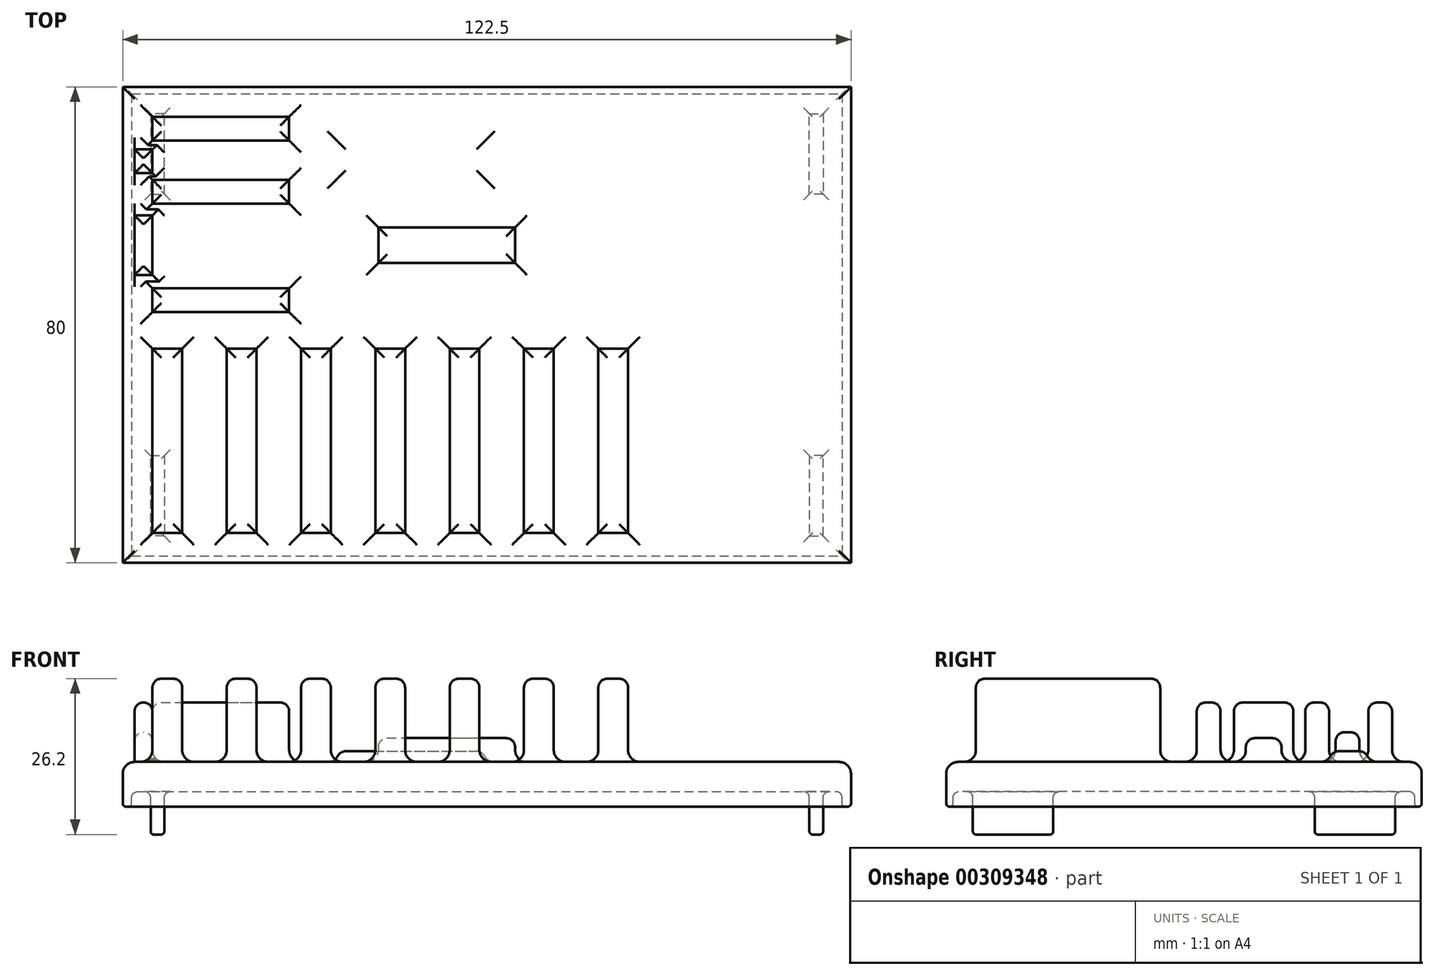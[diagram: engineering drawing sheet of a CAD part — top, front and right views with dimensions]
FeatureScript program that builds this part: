
annotation { "Feature Type Name" : "Feature", "Feature Type Description" : "" }
export const myFeature = defineFeature(function(context is Context, id is Id, definition is map)
    precondition{}
    {
        {
            var Q0;
            Q0=qCreatedBy(makeId("Top.planeOp"),FACE);
            var sketch = newSketch(context, id + "F0", { "sketchPlane" : qUnion([Q0])});
            skLineSegment(sketch, "E0.bottom", {"start": v(-61.25, 40) * mm, "end": v(61.25, 40) * mm});
            skLineSegment(sketch, "E0.top", {"start": v(-61.25, -40) * mm, "end": v(61.25, -40) * mm});
            skLineSegment(sketch, "E0.left", {"start": v(-61.25, 40) * mm, "end": v(-61.25, -40) * mm});
            skLineSegment(sketch, "E0.right", {"start": v(61.25, 40) * mm, "end": v(61.25, -40) * mm});
            skPoint(sketch, "E0.middle", {"position": v(0, 0) * mm});
            skLineSegment(sketch, "E1.bottom", {"start": v(-59.75, 38.85) * mm, "end": v(59.75, 38.85) * mm});
            skLineSegment(sketch, "E1.top", {"start": v(-59.75, -38.85) * mm, "end": v(59.75, -38.85) * mm});
            skLineSegment(sketch, "E1.left", {"start": v(-59.75, 38.85) * mm, "end": v(-59.75, -38.85) * mm});
            skLineSegment(sketch, "E1.right", {"start": v(59.75, 38.85) * mm, "end": v(59.75, -38.85) * mm});
            skLineSegment(sketch, "E2", {"start": v(61.25, -40) * mm, "end": v(61.25, -22) * mm});
            skLineSegment(sketch, "E3", {"start": v(61.25, -22) * mm, "end": v(54.25, -22) * mm});
            skLineSegment(sketch, "E4", {"start": v(54.25, -22) * mm, "end": v(54.25, -35.5) * mm});
            skLineSegment(sketch, "E5", {"start": v(54.25, -35.5) * mm, "end": v(56.55, -35.5) * mm});
            skLineSegment(sketch, "E6", {"start": v(56.55, -35.5) * mm, "end": v(56.55, -22) * mm});
            skLineSegment(sketch, "E7.MirrorCS", {"start": v(-56.55, -35.5) * mm, "end": v(-56.55, -22) * mm});
            skLineSegment(sketch, "E8.MirrorCS", {"start": v(-61.25, -22) * mm, "end": v(-54.25, -22) * mm});
            skLineSegment(sketch, "E9.MirrorCS", {"start": v(-54.25, -22) * mm, "end": v(-54.25, -35.5) * mm});
            skLineSegment(sketch, "E10.MirrorCS", {"start": v(-54.25, -35.5) * mm, "end": v(-56.55, -35.5) * mm});
            skLineSegment(sketch, "E11.MirrorCS", {"start": v(56.55, 35.5) * mm, "end": v(56.55, 22) * mm});
            skLineSegment(sketch, "E12.MirrorCS", {"start": v(54.25, 35.5) * mm, "end": v(56.55, 35.5) * mm});
            skLineSegment(sketch, "E13.MirrorCS", {"start": v(54.25, 22) * mm, "end": v(54.25, 35.5) * mm});
            skLineSegment(sketch, "E14.MirrorCS", {"start": v(-54.25, 35.5) * mm, "end": v(-56.55, 35.5) * mm});
            skLineSegment(sketch, "E15.MirrorCS", {"start": v(-54.25, 22) * mm, "end": v(-54.25, 35.5) * mm});
            skLineSegment(sketch, "E16.MirrorCS", {"start": v(-56.55, 35.5) * mm, "end": v(-56.55, 22) * mm});
            skLineSegment(sketch, "E17.MirrorCS", {"start": v(-61.25, 22) * mm, "end": v(-54.25, 22) * mm});
            skLineSegment(sketch, "E18.MirrorCS", {"start": v(61.25, 22) * mm, "end": v(54.25, 22) * mm});
            skSolve(sketch);
        }
        {
            var Q0;
            {var subQ0=sQuery(id+"F0.wireOp",EDGE,"E4");Q0=makeQuery(id+"F0.imprint","IMPRINT",FACE,{"disambiguationData":[TD([[makeQuery(id+"F0.imprint","IMPRINT",EDGE,{"derivedFrom":subQ0}),1.0]])]});}
            var Q1;
            {var subQ0=sQuery(id+"F0.wireOp",EDGE,"E9.MirrorCS");Q1=makeQuery(id+"F0.imprint","IMPRINT",FACE,{"disambiguationData":[TD([[makeQuery(id+"F0.imprint","IMPRINT",EDGE,{"derivedFrom":subQ0}),-1.0]])]});}
            var Q2;
            {var subQ0=sQuery(id+"F0.wireOp",EDGE,"E11.MirrorCS");Q2=makeQuery(id+"F0.imprint","IMPRINT",FACE,{"disambiguationData":[TD([[makeQuery(id+"F0.imprint","IMPRINT",EDGE,{"derivedFrom":subQ0}),-1.0]])]});}
            var Q3;
            Q3=makeQuery(id+"F0.imprint","IMPRINT",FACE,{"disambiguationData":[TD([[makeQuery(id+"F0.imprint","IMPRINT",EDGE,{"derivedFrom":sQuery(id+"F0.wireOp",EDGE,"E14.MirrorCS")}),1.0]])]});
            var Q4;
            {var subQ2=sQuery(id+"F0.wireOp",EDGE,"E0.bottom");Q4=makeQuery(id+"F0.imprint","IMPRINT",FACE,{"disambiguationData":[TD([[makeQuery(id+"F0.imprint","IMPRINT",EDGE,{"derivedFrom":subQ2}),-1.0]])]});}
            var Q5;
            {var subQ2=sQuery(id+"F0.wireOp",EDGE,"E0.top");Q5=makeQuery(id+"F0.imprint","IMPRINT",FACE,{"disambiguationData":[TD([[makeQuery(id+"F0.imprint","IMPRINT",EDGE,{"derivedFrom":subQ2}),1.0]])]});}
            var Q6;
            {var subQ0=sQuery(id+"F0.wireOp",EDGE,"E8.MirrorCS");var subQ1=sQuery(id+"F0.wireOp",EDGE,"E0.left");var subQ2=makeQuery(id+"F0.imprint","INTERSECT",VERTEX,{"derivedFrom":[subQ1,subQ0]});Q6=makeQuery(id+"F0.imprint","IMPRINT",FACE,{"disambiguationData":[TD([[makeQuery(id+"F0.imprint","IMPRINT",EDGE,{"disambiguationData":[TD([[subQ2,1.0]])],"derivedFrom":subQ1}),1.0]])]});}
            var Q7;
            {var subQ10=sQuery(id+"F0.wireOp",EDGE,"E1.bottom");Q7=makeQuery(id+"F0.imprint","IMPRINT",FACE,{"disambiguationData":[TD([[makeQuery(id+"F0.imprint","IMPRINT",EDGE,{"derivedFrom":subQ10}),-1.0]])]});}
            var Q8;
            {var subQ3=sQuery(id+"F0.wireOp",EDGE,"E18.MirrorCS");var subQ5=sQuery(id+"F0.wireOp",EDGE,"E1.right");var subQ7=makeQuery(id+"F0.imprint","INTERSECT",VERTEX,{"derivedFrom":[subQ5,subQ3]});Q8=makeQuery(id+"F0.imprint","IMPRINT",FACE,{"disambiguationData":[TD([[makeQuery(id+"F0.imprint","IMPRINT",EDGE,{"disambiguationData":[TD([[subQ7,-1.0]])],"derivedFrom":subQ5}),1.0]])]});}
            extrude(context, id + "F1", {"entities" : qUnion([Q0, Q1, Q2, Q3, Q4, Q5, Q6, Q7, Q8]), "oppositeDirection" : true, "depth" : 5 * mm});
        }
        {
            var Q0;
            {var subQ0=sQuery(id+"F0.wireOp",EDGE,"E9.MirrorCS");Q0=makeQuery(id+"F0.imprint","IMPRINT",FACE,{"disambiguationData":[TD([[makeQuery(id+"F0.imprint","IMPRINT",EDGE,{"derivedFrom":subQ0}),-1.0]])]});}
            var Q1;
            Q1=makeQuery(id+"F0.imprint","IMPRINT",FACE,{"disambiguationData":[TD([[makeQuery(id+"F0.imprint","IMPRINT",EDGE,{"derivedFrom":sQuery(id+"F0.wireOp",EDGE,"E14.MirrorCS")}),1.0]])]});
            var Q2;
            {var subQ0=sQuery(id+"F0.wireOp",EDGE,"E11.MirrorCS");Q2=makeQuery(id+"F0.imprint","IMPRINT",FACE,{"disambiguationData":[TD([[makeQuery(id+"F0.imprint","IMPRINT",EDGE,{"derivedFrom":subQ0}),-1.0]])]});}
            var Q3;
            {var subQ0=sQuery(id+"F0.wireOp",EDGE,"E4");Q3=makeQuery(id+"F0.imprint","IMPRINT",FACE,{"disambiguationData":[TD([[makeQuery(id+"F0.imprint","IMPRINT",EDGE,{"derivedFrom":subQ0}),1.0]])]});}
            extrude(context, id + "F2", {"entities" : qUnion([Q0, Q1, Q2, Q3]), "operationType" : NewBodyOperationType.ADD, "oppositeDirection" : true, "depth" : (7.2 + 5) * mm});
        }
        {
            var Q0;
            {var subQ0=sQuery(id+"F0.wireOp",EDGE,"E8.MirrorCS");var subQ1=sQuery(id+"F0.wireOp",EDGE,"E0.left");var subQ2=makeQuery(id+"F0.imprint","INTERSECT",VERTEX,{"derivedFrom":[subQ1,subQ0]});Q0=makeQuery(id+"F0.imprint","IMPRINT",FACE,{"disambiguationData":[TD([[makeQuery(id+"F0.imprint","IMPRINT",EDGE,{"disambiguationData":[TD([[subQ2,1.0]])],"derivedFrom":subQ1}),1.0]])]});}
            var Q1;
            {var subQ2=sQuery(id+"F0.wireOp",EDGE,"E0.bottom");Q1=makeQuery(id+"F0.imprint","IMPRINT",FACE,{"disambiguationData":[TD([[makeQuery(id+"F0.imprint","IMPRINT",EDGE,{"derivedFrom":subQ2}),-1.0]])]});}
            var Q2;
            {var subQ2=sQuery(id+"F0.wireOp",EDGE,"E0.top");Q2=makeQuery(id+"F0.imprint","IMPRINT",FACE,{"disambiguationData":[TD([[makeQuery(id+"F0.imprint","IMPRINT",EDGE,{"derivedFrom":subQ2}),1.0]])]});}
            var Q3;
            {var subQ3=sQuery(id+"F0.wireOp",EDGE,"E18.MirrorCS");var subQ5=sQuery(id+"F0.wireOp",EDGE,"E1.right");var subQ7=makeQuery(id+"F0.imprint","INTERSECT",VERTEX,{"derivedFrom":[subQ5,subQ3]});Q3=makeQuery(id+"F0.imprint","IMPRINT",FACE,{"disambiguationData":[TD([[makeQuery(id+"F0.imprint","IMPRINT",EDGE,{"disambiguationData":[TD([[subQ7,-1.0]])],"derivedFrom":subQ5}),1.0]])]});}
            extrude(context, id + "F3", {"entities" : qUnion([Q0, Q1, Q2, Q3]), "operationType" : NewBodyOperationType.ADD, "oppositeDirection" : true, "depth" : (2.5 + 5) * mm});
        }
        {
            var Q0;
            Q0=makeQuery(id+"F1.opExtrude","CAP_FACE",FACE,{"disambiguationData":[OSD([sQuery(id+"F0.wireOp",EDGE,"E0.bottom"),sQuery(id+"F0.wireOp",EDGE,"E0.top"),sQuery(id+"F0.wireOp",EDGE,"E0.left"),sQuery(id+"F0.wireOp",EDGE,"E0.right"),sQuery(id+"F0.wireOp",EDGE,"E2")])],"isStart":true});
            fillet(context, id + "F4", {"entities" : qUnion([Q0]), "radius" : 2 * mm, "tangentPropagation" : true, "allowEdgeOverflow" : false});
        }
        {
            var Q0;
            Q0=makeQuery(id+"F2.opExtrude","CAP_FACE",FACE,{"disambiguationData":[OSD([sQuery(id+"F0.wireOp",EDGE,"E8.MirrorCS"),sQuery(id+"F0.wireOp",EDGE,"E9.MirrorCS"),sQuery(id+"F0.wireOp",EDGE,"E10.MirrorCS"),sQuery(id+"F0.wireOp",EDGE,"E7.MirrorCS")])],"isStart":false});
            var Q1;
            Q1=makeQuery(id+"F3.opExtrude","CAP_FACE",FACE,{"disambiguationData":[OSD([sQuery(id+"F0.wireOp",EDGE,"E0.bottom"),sQuery(id+"F0.wireOp",EDGE,"E0.top"),sQuery(id+"F0.wireOp",EDGE,"E0.left"),sQuery(id+"F0.wireOp",EDGE,"E0.right"),sQuery(id+"F0.wireOp",EDGE,"E1.bottom"),sQuery(id+"F0.wireOp",EDGE,"E1.top"),sQuery(id+"F0.wireOp",EDGE,"E1.left"),sQuery(id+"F0.wireOp",EDGE,"E1.right"),sQuery(id+"F0.wireOp",EDGE,"E2")])],"isStart":false});
            var Q2;
            Q2=makeQuery(id+"F2.opExtrude","CAP_FACE",FACE,{"disambiguationData":[OSD([sQuery(id+"F0.wireOp",EDGE,"E14.MirrorCS"),sQuery(id+"F0.wireOp",EDGE,"E16.MirrorCS"),sQuery(id+"F0.wireOp",EDGE,"E15.MirrorCS"),sQuery(id+"F0.wireOp",EDGE,"E17.MirrorCS")])],"isStart":false});
            var Q3;
            Q3=makeQuery(id+"F2.opExtrude","CAP_FACE",FACE,{"disambiguationData":[OSD([sQuery(id+"F0.wireOp",EDGE,"E11.MirrorCS"),sQuery(id+"F0.wireOp",EDGE,"E12.MirrorCS"),sQuery(id+"F0.wireOp",EDGE,"E13.MirrorCS"),sQuery(id+"F0.wireOp",EDGE,"E18.MirrorCS")])],"isStart":false});
            var Q4;
            Q4=makeQuery(id+"F2.opExtrude","CAP_FACE",FACE,{"disambiguationData":[OSD([sQuery(id+"F0.wireOp",EDGE,"E3"),sQuery(id+"F0.wireOp",EDGE,"E4"),sQuery(id+"F0.wireOp",EDGE,"E5"),sQuery(id+"F0.wireOp",EDGE,"E6")])],"isStart":false});
            fillet(context, id + "F5", {"entities" : qUnion([Q0, Q1, Q2, Q3, Q4]), "radius" : .5 * mm, "tangentPropagation" : true, "allowEdgeOverflow" : false});
        }
        {
            var Q0;
            Q0=makeQuery(id+"F2.boolean.opBoolean","INTERSECT",EDGE,{"derivedFrom":[makeQuery(id+"F1.opExtrude","CAP_FACE",FACE,{"disambiguationData":[OSD([sQuery(id+"F0.wireOp",EDGE,"E0.bottom"),sQuery(id+"F0.wireOp",EDGE,"E0.top"),sQuery(id+"F0.wireOp",EDGE,"E0.left"),sQuery(id+"F0.wireOp",EDGE,"E0.right"),sQuery(id+"F0.wireOp",EDGE,"E2")])],"isStart":false}),makeQuery(id+"F2.opExtrude","SWEPT_FACE",FACE,{"disambiguationData":[OSD([sQuery(id+"F0.wireOp",EDGE,"E9.MirrorCS")])]})]});
            var Q1;
            Q1=makeQuery(id+"F2.boolean.opBoolean","INTERSECT",EDGE,{"derivedFrom":[makeQuery(id+"F1.opExtrude","CAP_FACE",FACE,{"disambiguationData":[OSD([sQuery(id+"F0.wireOp",EDGE,"E0.bottom"),sQuery(id+"F0.wireOp",EDGE,"E0.top"),sQuery(id+"F0.wireOp",EDGE,"E0.left"),sQuery(id+"F0.wireOp",EDGE,"E0.right"),sQuery(id+"F0.wireOp",EDGE,"E2")])],"isStart":false}),makeQuery(id+"F2.opExtrude","SWEPT_FACE",FACE,{"disambiguationData":[OSD([sQuery(id+"F0.wireOp",EDGE,"E8.MirrorCS")])]})]});
            var Q2;
            Q2=makeQuery(id+"F2.boolean.opBoolean","INTERSECT",EDGE,{"derivedFrom":[makeQuery(id+"F1.opExtrude","CAP_FACE",FACE,{"disambiguationData":[OSD([sQuery(id+"F0.wireOp",EDGE,"E0.bottom"),sQuery(id+"F0.wireOp",EDGE,"E0.top"),sQuery(id+"F0.wireOp",EDGE,"E0.left"),sQuery(id+"F0.wireOp",EDGE,"E0.right"),sQuery(id+"F0.wireOp",EDGE,"E2")])],"isStart":false}),makeQuery(id+"F2.opExtrude","SWEPT_FACE",FACE,{"disambiguationData":[OSD([sQuery(id+"F0.wireOp",EDGE,"E7.MirrorCS")])]})]});
            var Q3;
            Q3=makeQuery(id+"F2.boolean.opBoolean","INTERSECT",EDGE,{"derivedFrom":[makeQuery(id+"F1.opExtrude","CAP_FACE",FACE,{"disambiguationData":[OSD([sQuery(id+"F0.wireOp",EDGE,"E0.bottom"),sQuery(id+"F0.wireOp",EDGE,"E0.top"),sQuery(id+"F0.wireOp",EDGE,"E0.left"),sQuery(id+"F0.wireOp",EDGE,"E0.right"),sQuery(id+"F0.wireOp",EDGE,"E2")])],"isStart":false}),makeQuery(id+"F2.opExtrude","SWEPT_FACE",FACE,{"disambiguationData":[OSD([sQuery(id+"F0.wireOp",EDGE,"E10.MirrorCS")])]})]});
            var Q4;
            Q4=makeQuery(id+"F2.boolean.opBoolean","INTERSECT",EDGE,{"derivedFrom":[makeQuery(id+"F1.opExtrude","CAP_FACE",FACE,{"disambiguationData":[OSD([sQuery(id+"F0.wireOp",EDGE,"E0.bottom"),sQuery(id+"F0.wireOp",EDGE,"E0.top"),sQuery(id+"F0.wireOp",EDGE,"E0.left"),sQuery(id+"F0.wireOp",EDGE,"E0.right"),sQuery(id+"F0.wireOp",EDGE,"E2")])],"isStart":false}),makeQuery(id+"F2.opExtrude","SWEPT_FACE",FACE,{"disambiguationData":[OSD([sQuery(id+"F0.wireOp",EDGE,"E16.MirrorCS")])]})]});
            var Q5;
            Q5=makeQuery(id+"F2.boolean.opBoolean","INTERSECT",EDGE,{"derivedFrom":[makeQuery(id+"F1.opExtrude","CAP_FACE",FACE,{"disambiguationData":[OSD([sQuery(id+"F0.wireOp",EDGE,"E0.bottom"),sQuery(id+"F0.wireOp",EDGE,"E0.top"),sQuery(id+"F0.wireOp",EDGE,"E0.left"),sQuery(id+"F0.wireOp",EDGE,"E0.right"),sQuery(id+"F0.wireOp",EDGE,"E2")])],"isStart":false}),makeQuery(id+"F2.opExtrude","SWEPT_FACE",FACE,{"disambiguationData":[OSD([sQuery(id+"F0.wireOp",EDGE,"E17.MirrorCS")])]})]});
            var Q6;
            Q6=makeQuery(id+"F2.boolean.opBoolean","INTERSECT",EDGE,{"derivedFrom":[makeQuery(id+"F1.opExtrude","CAP_FACE",FACE,{"disambiguationData":[OSD([sQuery(id+"F0.wireOp",EDGE,"E0.bottom"),sQuery(id+"F0.wireOp",EDGE,"E0.top"),sQuery(id+"F0.wireOp",EDGE,"E0.left"),sQuery(id+"F0.wireOp",EDGE,"E0.right"),sQuery(id+"F0.wireOp",EDGE,"E2")])],"isStart":false}),makeQuery(id+"F2.opExtrude","SWEPT_FACE",FACE,{"disambiguationData":[OSD([sQuery(id+"F0.wireOp",EDGE,"E15.MirrorCS")])]})]});
            var Q7;
            Q7=makeQuery(id+"F2.boolean.opBoolean","INTERSECT",EDGE,{"derivedFrom":[makeQuery(id+"F1.opExtrude","CAP_FACE",FACE,{"disambiguationData":[OSD([sQuery(id+"F0.wireOp",EDGE,"E0.bottom"),sQuery(id+"F0.wireOp",EDGE,"E0.top"),sQuery(id+"F0.wireOp",EDGE,"E0.left"),sQuery(id+"F0.wireOp",EDGE,"E0.right"),sQuery(id+"F0.wireOp",EDGE,"E2")])],"isStart":false}),makeQuery(id+"F2.opExtrude","SWEPT_FACE",FACE,{"disambiguationData":[OSD([sQuery(id+"F0.wireOp",EDGE,"E14.MirrorCS")])]})]});
            var Q8;
            Q8=makeQuery(id+"F2.boolean.opBoolean","INTERSECT",EDGE,{"derivedFrom":[makeQuery(id+"F1.opExtrude","CAP_FACE",FACE,{"disambiguationData":[OSD([sQuery(id+"F0.wireOp",EDGE,"E0.bottom"),sQuery(id+"F0.wireOp",EDGE,"E0.top"),sQuery(id+"F0.wireOp",EDGE,"E0.left"),sQuery(id+"F0.wireOp",EDGE,"E0.right"),sQuery(id+"F0.wireOp",EDGE,"E2")])],"isStart":false}),makeQuery(id+"F2.opExtrude","SWEPT_FACE",FACE,{"disambiguationData":[OSD([sQuery(id+"F0.wireOp",EDGE,"E13.MirrorCS")])]})]});
            var Q9;
            Q9=makeQuery(id+"F2.boolean.opBoolean","INTERSECT",EDGE,{"derivedFrom":[makeQuery(id+"F1.opExtrude","CAP_FACE",FACE,{"disambiguationData":[OSD([sQuery(id+"F0.wireOp",EDGE,"E0.bottom"),sQuery(id+"F0.wireOp",EDGE,"E0.top"),sQuery(id+"F0.wireOp",EDGE,"E0.left"),sQuery(id+"F0.wireOp",EDGE,"E0.right"),sQuery(id+"F0.wireOp",EDGE,"E2")])],"isStart":false}),makeQuery(id+"F2.opExtrude","SWEPT_FACE",FACE,{"disambiguationData":[OSD([sQuery(id+"F0.wireOp",EDGE,"E12.MirrorCS")])]})]});
            var Q10;
            Q10=makeQuery(id+"F2.boolean.opBoolean","INTERSECT",EDGE,{"derivedFrom":[makeQuery(id+"F1.opExtrude","CAP_FACE",FACE,{"disambiguationData":[OSD([sQuery(id+"F0.wireOp",EDGE,"E0.bottom"),sQuery(id+"F0.wireOp",EDGE,"E0.top"),sQuery(id+"F0.wireOp",EDGE,"E0.left"),sQuery(id+"F0.wireOp",EDGE,"E0.right"),sQuery(id+"F0.wireOp",EDGE,"E2")])],"isStart":false}),makeQuery(id+"F2.opExtrude","SWEPT_FACE",FACE,{"disambiguationData":[OSD([sQuery(id+"F0.wireOp",EDGE,"E11.MirrorCS")])]})]});
            var Q11;
            Q11=makeQuery(id+"F2.boolean.opBoolean","INTERSECT",EDGE,{"derivedFrom":[makeQuery(id+"F1.opExtrude","CAP_FACE",FACE,{"disambiguationData":[OSD([sQuery(id+"F0.wireOp",EDGE,"E0.bottom"),sQuery(id+"F0.wireOp",EDGE,"E0.top"),sQuery(id+"F0.wireOp",EDGE,"E0.left"),sQuery(id+"F0.wireOp",EDGE,"E0.right"),sQuery(id+"F0.wireOp",EDGE,"E2")])],"isStart":false}),makeQuery(id+"F2.opExtrude","SWEPT_FACE",FACE,{"disambiguationData":[OSD([sQuery(id+"F0.wireOp",EDGE,"E18.MirrorCS")])]})]});
            var Q12;
            Q12=makeQuery(id+"F2.boolean.opBoolean","INTERSECT",EDGE,{"derivedFrom":[makeQuery(id+"F1.opExtrude","CAP_FACE",FACE,{"disambiguationData":[OSD([sQuery(id+"F0.wireOp",EDGE,"E0.bottom"),sQuery(id+"F0.wireOp",EDGE,"E0.top"),sQuery(id+"F0.wireOp",EDGE,"E0.left"),sQuery(id+"F0.wireOp",EDGE,"E0.right"),sQuery(id+"F0.wireOp",EDGE,"E2")])],"isStart":false}),makeQuery(id+"F2.opExtrude","SWEPT_FACE",FACE,{"disambiguationData":[OSD([sQuery(id+"F0.wireOp",EDGE,"E5")])]})]});
            var Q13;
            Q13=makeQuery(id+"F2.boolean.opBoolean","INTERSECT",EDGE,{"derivedFrom":[makeQuery(id+"F1.opExtrude","CAP_FACE",FACE,{"disambiguationData":[OSD([sQuery(id+"F0.wireOp",EDGE,"E0.bottom"),sQuery(id+"F0.wireOp",EDGE,"E0.top"),sQuery(id+"F0.wireOp",EDGE,"E0.left"),sQuery(id+"F0.wireOp",EDGE,"E0.right"),sQuery(id+"F0.wireOp",EDGE,"E2")])],"isStart":false}),makeQuery(id+"F2.opExtrude","SWEPT_FACE",FACE,{"disambiguationData":[OSD([sQuery(id+"F0.wireOp",EDGE,"E6")])]})]});
            var Q14;
            Q14=makeQuery(id+"F2.boolean.opBoolean","INTERSECT",EDGE,{"derivedFrom":[makeQuery(id+"F1.opExtrude","CAP_FACE",FACE,{"disambiguationData":[OSD([sQuery(id+"F0.wireOp",EDGE,"E0.bottom"),sQuery(id+"F0.wireOp",EDGE,"E0.top"),sQuery(id+"F0.wireOp",EDGE,"E0.left"),sQuery(id+"F0.wireOp",EDGE,"E0.right"),sQuery(id+"F0.wireOp",EDGE,"E2")])],"isStart":false}),makeQuery(id+"F2.opExtrude","SWEPT_FACE",FACE,{"disambiguationData":[OSD([sQuery(id+"F0.wireOp",EDGE,"E4")])]})]});
            var Q15;
            Q15=makeQuery(id+"F2.boolean.opBoolean","INTERSECT",EDGE,{"derivedFrom":[makeQuery(id+"F1.opExtrude","CAP_FACE",FACE,{"disambiguationData":[OSD([sQuery(id+"F0.wireOp",EDGE,"E0.bottom"),sQuery(id+"F0.wireOp",EDGE,"E0.top"),sQuery(id+"F0.wireOp",EDGE,"E0.left"),sQuery(id+"F0.wireOp",EDGE,"E0.right"),sQuery(id+"F0.wireOp",EDGE,"E2")])],"isStart":false}),makeQuery(id+"F2.opExtrude","SWEPT_FACE",FACE,{"disambiguationData":[OSD([sQuery(id+"F0.wireOp",EDGE,"E3")])]})]});
            var Q16;
            Q16=makeQuery(id+"F1.opExtrude","CAP_FACE",FACE,{"disambiguationData":[OSD([sQuery(id+"F0.wireOp",EDGE,"E0.bottom"),sQuery(id+"F0.wireOp",EDGE,"E0.top"),sQuery(id+"F0.wireOp",EDGE,"E0.left"),sQuery(id+"F0.wireOp",EDGE,"E0.right"),sQuery(id+"F0.wireOp",EDGE,"E2")])],"isStart":false});
            fillet(context, id + "F6", {"entities" : qUnion([Q0, Q1, Q2, Q3, Q4, Q5, Q6, Q7, Q8, Q9, Q10, Q11, Q12, Q13, Q14, Q15, Q16]), "radius" : 1 * mm, "tangentPropagation" : true, "allowEdgeOverflow" : false});
        }
        {
            var Q0;
            Q0=qCreatedBy(makeId("Top.planeOp"),FACE);
            var sketch = newSketch(context, id + "F7", { "sketchPlane" : qUnion([Q0])});
            skLineSegment(sketch, "E19", {"start": v(-61.25, 40) * mm, "end": v(-61.25, 35) * mm});
            skLineSegment(sketch, "E20", {"start": v(-61.25, 35) * mm, "end": v(-56.25, 35) * mm});
            skLineSegment(sketch, "E21.bottom", {"start": v(-56.25, 35) * mm, "end": v(-33.25, 35) * mm});
            skLineSegment(sketch, "E21.top", {"start": v(-56.25, 31) * mm, "end": v(-33.25, 31) * mm});
            skLineSegment(sketch, "E21.left", {"start": v(-56.25, 35) * mm, "end": v(-56.25, 31) * mm});
            skLineSegment(sketch, "E21.right", {"start": v(-33.25, 35) * mm, "end": v(-33.25, 31) * mm});
            skLineSegment(sketch, "E22", {"start": v(-56.25, 31) * mm, "end": v(-56.25, 24.4) * mm});
            skLineSegment(sketch, "E23.bottom", {"start": v(-56.25, 24.4) * mm, "end": v(-33.25, 24.4) * mm});
            skLineSegment(sketch, "E23.top", {"start": v(-56.25, 20.4) * mm, "end": v(-33.25, 20.4) * mm});
            skLineSegment(sketch, "E23.left", {"start": v(-56.25, 24.4) * mm, "end": v(-56.25, 20.4) * mm});
            skLineSegment(sketch, "E23.right", {"start": v(-33.25, 24.4) * mm, "end": v(-33.25, 20.4) * mm});
            skLineSegment(sketch, "E24", {"start": v(-33.25, 31) * mm, "end": v(-25.25, 31) * mm});
            skLineSegment(sketch, "E25.bottom", {"start": v(-25.25, 31) * mm, "end": v(-0.25, 31) * mm});
            skLineSegment(sketch, "E25.top", {"start": v(-25.25, 24.5) * mm, "end": v(-0.25, 24.5) * mm});
            skLineSegment(sketch, "E25.left", {"start": v(-25.25, 31) * mm, "end": v(-25.25, 24.5) * mm});
            skLineSegment(sketch, "E25.right", {"start": v(-0.25, 31) * mm, "end": v(-0.25, 24.5) * mm});
            skLineSegment(sketch, "E26", {"start": v(-56.25, 20.4) * mm, "end": v(-56.25, 6.15) * mm});
            skLineSegment(sketch, "E27.bottom", {"start": v(-56.25, 6.15) * mm, "end": v(-33.25, 6.15) * mm});
            skLineSegment(sketch, "E27.top", {"start": v(-56.25, 2.15) * mm, "end": v(-33.25, 2.15) * mm});
            skLineSegment(sketch, "E27.left", {"start": v(-56.25, 6.15) * mm, "end": v(-56.25, 2.15) * mm});
            skLineSegment(sketch, "E27.right", {"start": v(-33.25, 6.15) * mm, "end": v(-33.25, 2.15) * mm});
            skLineSegment(sketch, "E28", {"start": v(-33.25, 20.4) * mm, "end": v(-18.25, 20.4) * mm});
            skLineSegment(sketch, "E29", {"start": v(-18.25, 20.4) * mm, "end": v(-18.25, 16.4) * mm});
            skLineSegment(sketch, "E30.bottom", {"start": v(-18.25, 16.4) * mm, "end": v(4.75, 16.4) * mm});
            skLineSegment(sketch, "E30.top", {"start": v(-18.25, 10.4) * mm, "end": v(4.75, 10.4) * mm});
            skLineSegment(sketch, "E30.left", {"start": v(-18.25, 16.4) * mm, "end": v(-18.25, 10.4) * mm});
            skLineSegment(sketch, "E30.right", {"start": v(4.75, 16.4) * mm, "end": v(4.75, 10.4) * mm});
            skLineSegment(sketch, "E31.bottom", {"start": v(-59.25, 18.4) * mm, "end": v(-56.25, 18.4) * mm});
            skLineSegment(sketch, "E31.top", {"start": v(-59.25, 8.4) * mm, "end": v(-56.25, 8.4) * mm});
            skLineSegment(sketch, "E31.left", {"start": v(-59.25, 18.4) * mm, "end": v(-59.25, 8.4) * mm});
            skLineSegment(sketch, "E31.right", {"start": v(-56.25, 18.4) * mm, "end": v(-56.25, 8.4) * mm});
            skLineSegment(sketch, "E32", {"start": v(-56.25, 20.4) * mm, "end": v(-56.25, 18.4) * mm});
            skLineSegment(sketch, "E33", {"start": v(-61.25, -40) * mm, "end": v(-61.25, -35) * mm});
            skLineSegment(sketch, "E34", {"start": v(-61.25, -35) * mm, "end": v(-56.25, -35) * mm});
            skLineSegment(sketch, "E35.bottom", {"start": v(-56.25, -35) * mm, "end": v(-51.25, -35) * mm});
            skLineSegment(sketch, "E35.top", {"start": v(-56.25, -4) * mm, "end": v(-51.25, -4) * mm});
            skLineSegment(sketch, "E35.left", {"start": v(-56.25, -35) * mm, "end": v(-56.25, -4) * mm});
            skLineSegment(sketch, "E35.right", {"start": v(-51.25, -35) * mm, "end": v(-51.25, -4) * mm});
            skLineSegment(sketch, "E36", {"start": v(-51.25, -35) * mm, "end": v(-43.75, -35) * mm});
            skLineSegment(sketch, "E37.bottom", {"start": v(-43.75, -35) * mm, "end": v(-38.75, -35) * mm});
            skLineSegment(sketch, "E37.top", {"start": v(-43.75, -4) * mm, "end": v(-38.75, -4) * mm});
            skLineSegment(sketch, "E37.left", {"start": v(-43.75, -35) * mm, "end": v(-43.75, -4) * mm});
            skLineSegment(sketch, "E37.right", {"start": v(-38.75, -35) * mm, "end": v(-38.75, -4) * mm});
            skLineSegment(sketch, "E38", {"start": v(-38.75, -35) * mm, "end": v(-31.25, -35) * mm});
            skLineSegment(sketch, "E39.bottom", {"start": v(-31.25, -35) * mm, "end": v(-26.25, -35) * mm});
            skLineSegment(sketch, "E39.top", {"start": v(-31.25, -4) * mm, "end": v(-26.25, -4) * mm});
            skLineSegment(sketch, "E39.left", {"start": v(-31.25, -35) * mm, "end": v(-31.25, -4) * mm});
            skLineSegment(sketch, "E39.right", {"start": v(-26.25, -35) * mm, "end": v(-26.25, -4) * mm});
            skLineSegment(sketch, "E40", {"start": v(-26.25, -35) * mm, "end": v(-18.75, -35) * mm});
            skLineSegment(sketch, "E41.bottom", {"start": v(-18.75, -35) * mm, "end": v(-13.75, -35) * mm});
            skLineSegment(sketch, "E41.top", {"start": v(-18.75, -4) * mm, "end": v(-13.75, -4) * mm});
            skLineSegment(sketch, "E41.left", {"start": v(-18.75, -35) * mm, "end": v(-18.75, -4) * mm});
            skLineSegment(sketch, "E41.right", {"start": v(-13.75, -35) * mm, "end": v(-13.75, -4) * mm});
            skLineSegment(sketch, "E42", {"start": v(-13.75, -35) * mm, "end": v(-6.25, -35) * mm});
            skLineSegment(sketch, "E43.bottom", {"start": v(-6.25, -35) * mm, "end": v(-1.25, -35) * mm});
            skLineSegment(sketch, "E43.top", {"start": v(-6.25, -4) * mm, "end": v(-1.25, -4) * mm});
            skLineSegment(sketch, "E43.left", {"start": v(-6.25, -35) * mm, "end": v(-6.25, -4) * mm});
            skLineSegment(sketch, "E43.right", {"start": v(-1.25, -35) * mm, "end": v(-1.25, -4) * mm});
            skLineSegment(sketch, "E44", {"start": v(-1.25, -35) * mm, "end": v(6.25, -35) * mm});
            skLineSegment(sketch, "E45.bottom", {"start": v(6.25, -35) * mm, "end": v(11.25, -35) * mm});
            skLineSegment(sketch, "E45.top", {"start": v(6.25, -4) * mm, "end": v(11.25, -4) * mm});
            skLineSegment(sketch, "E45.left", {"start": v(6.25, -35) * mm, "end": v(6.25, -4) * mm});
            skLineSegment(sketch, "E45.right", {"start": v(11.25, -35) * mm, "end": v(11.25, -4) * mm});
            skLineSegment(sketch, "E46", {"start": v(11.25, -35) * mm, "end": v(18.75, -35) * mm});
            skLineSegment(sketch, "E47.bottom", {"start": v(18.75, -35) * mm, "end": v(23.75, -35) * mm});
            skLineSegment(sketch, "E47.top", {"start": v(18.75, -4) * mm, "end": v(23.75, -4) * mm});
            skLineSegment(sketch, "E47.left", {"start": v(18.75, -35) * mm, "end": v(18.75, -4) * mm});
            skLineSegment(sketch, "E47.right", {"start": v(23.75, -35) * mm, "end": v(23.75, -4) * mm});
            skLineSegment(sketch, "E48.bottom", {"start": v(-56.25, 29.5) * mm, "end": v(-59.25, 29.5) * mm});
            skLineSegment(sketch, "E48.top", {"start": v(-56.25, 25.5) * mm, "end": v(-59.25, 25.5) * mm});
            skLineSegment(sketch, "E48.left", {"start": v(-56.25, 29.5) * mm, "end": v(-56.25, 25.5) * mm});
            skLineSegment(sketch, "E48.right", {"start": v(-59.25, 29.5) * mm, "end": v(-59.25, 25.5) * mm});
            skLineSegment(sketch, "E49", {"start": v(-56.25, 31) * mm, "end": v(-56.25, 29.5) * mm});
            skSolve(sketch);
        }
        {
            var Q0;
            Q0=makeQuery(id+"F7.imprint","IMPRINT",FACE,{"disambiguationData":[TD([[makeQuery(id+"F7.imprint","IMPRINT",EDGE,{"derivedFrom":sQuery(id+"F7.wireOp",EDGE,"RmiUNKtS-Ojf3-qw3z-NKSH-yDlJa6DSz4qu.bottom")}),-1.0]])]});
            var Q1;
            Q1=makeQuery(id+"F7.imprint","IMPRINT",FACE,{"disambiguationData":[TD([[makeQuery(id+"F7.imprint","IMPRINT",EDGE,{"derivedFrom":sQuery(id+"F7.wireOp",EDGE,"E25.bottom")}),-1.0]])]});
            extrude(context, id + "F8", {"entities" : qUnion([Q0, Q1]), "operationType" : NewBodyOperationType.ADD, "depth" : 1.8 * mm});
        }
        {
            var Q0;
            Q0=makeQuery(id+"F7.imprint","IMPRINT",FACE,{"disambiguationData":[TD([[makeQuery(id+"F7.imprint","IMPRINT",EDGE,{"derivedFrom":sQuery(id+"F7.wireOp",EDGE,"E48.bottom")}),1.0]])]});
            extrude(context, id + "F9", {"entities" : qUnion([Q0]), "operationType" : NewBodyOperationType.ADD, "depth" : 5 * mm});
        }
        {
            var Q0;
            Q0=makeQuery(id+"F7.imprint","IMPRINT",FACE,{"disambiguationData":[TD([[makeQuery(id+"F7.imprint","IMPRINT",EDGE,{"derivedFrom":sQuery(id+"F7.wireOp",EDGE,"E35.bottom")}),1.0]])]});
            var Q1;
            Q1=makeQuery(id+"F7.imprint","IMPRINT",FACE,{"disambiguationData":[TD([[makeQuery(id+"F7.imprint","IMPRINT",EDGE,{"derivedFrom":sQuery(id+"F7.wireOp",EDGE,"E37.bottom")}),1.0]])]});
            var Q2;
            Q2=makeQuery(id+"F7.imprint","IMPRINT",FACE,{"disambiguationData":[TD([[makeQuery(id+"F7.imprint","IMPRINT",EDGE,{"derivedFrom":sQuery(id+"F7.wireOp",EDGE,"E39.bottom")}),1.0]])]});
            var Q3;
            Q3=makeQuery(id+"F7.imprint","IMPRINT",FACE,{"disambiguationData":[TD([[makeQuery(id+"F7.imprint","IMPRINT",EDGE,{"derivedFrom":sQuery(id+"F7.wireOp",EDGE,"E41.bottom")}),1.0]])]});
            var Q4;
            Q4=makeQuery(id+"F7.imprint","IMPRINT",FACE,{"disambiguationData":[TD([[makeQuery(id+"F7.imprint","IMPRINT",EDGE,{"derivedFrom":sQuery(id+"F7.wireOp",EDGE,"E43.bottom")}),1.0]])]});
            var Q5;
            Q5=makeQuery(id+"F7.imprint","IMPRINT",FACE,{"disambiguationData":[TD([[makeQuery(id+"F7.imprint","IMPRINT",EDGE,{"derivedFrom":sQuery(id+"F7.wireOp",EDGE,"E45.bottom")}),1.0]])]});
            var Q6;
            Q6=makeQuery(id+"F7.imprint","IMPRINT",FACE,{"disambiguationData":[TD([[makeQuery(id+"F7.imprint","IMPRINT",EDGE,{"derivedFrom":sQuery(id+"F7.wireOp",EDGE,"E47.bottom")}),1.0]])]});
            extrude(context, id + "F10", {"entities" : qUnion([Q0, Q1, Q2, Q3, Q4, Q5, Q6]), "operationType" : NewBodyOperationType.ADD, "depth" : 14 * mm});
        }
        {
            var Q0;
            Q0=makeQuery(id+"F7.imprint","IMPRINT",FACE,{"disambiguationData":[TD([[makeQuery(id+"F7.imprint","IMPRINT",EDGE,{"derivedFrom":sQuery(id+"F7.wireOp",EDGE,"E23.bottom")}),-1.0]])]});
            var Q1;
            Q1=makeQuery(id+"F7.imprint","IMPRINT",FACE,{"disambiguationData":[TD([[makeQuery(id+"F7.imprint","IMPRINT",EDGE,{"derivedFrom":sQuery(id+"F7.wireOp",EDGE,"E27.bottom")}),-1.0]])]});
            var Q2;
            Q2=makeQuery(id+"F7.imprint","IMPRINT",FACE,{"disambiguationData":[TD([[makeQuery(id+"F7.imprint","IMPRINT",EDGE,{"derivedFrom":sQuery(id+"F7.wireOp",EDGE,"E31.bottom")}),-1.0]])]});
            var Q3;
            Q3=makeQuery(id+"F7.imprint","IMPRINT",FACE,{"disambiguationData":[TD([[makeQuery(id+"F7.imprint","IMPRINT",EDGE,{"derivedFrom":sQuery(id+"F7.wireOp",EDGE,"E21.bottom")}),-1.0]])]});
            extrude(context, id + "F11", {"entities" : qUnion([Q0, Q1, Q2, Q3]), "operationType" : NewBodyOperationType.ADD, "depth" : 10 * mm});
        }
        {
            var Q0;
            Q0=makeQuery(id+"F7.imprint","IMPRINT",FACE,{"disambiguationData":[TD([[makeQuery(id+"F7.imprint","IMPRINT",EDGE,{"derivedFrom":sQuery(id+"F7.wireOp",EDGE,"E30.bottom")}),-1.0]])]});
            extrude(context, id + "F12", {"entities" : qUnion([Q0]), "operationType" : NewBodyOperationType.ADD, "depth" : 4 * mm});
        }
        {
            var Q0;
            Q0=makeQuery(id+"F8.opExtrude","CAP_FACE",FACE,{"disambiguationData":[OSD([sQuery(id+"F7.wireOp",EDGE,"E25.bottom"),sQuery(id+"F7.wireOp",EDGE,"E25.top"),sQuery(id+"F7.wireOp",EDGE,"E25.left"),sQuery(id+"F7.wireOp",EDGE,"E25.right")])],"isStart":false});
            var Q1;
            Q1=makeQuery(id+"F12.opExtrude","CAP_FACE",FACE,{"disambiguationData":[OSD([sQuery(id+"F7.wireOp",EDGE,"E30.bottom"),sQuery(id+"F7.wireOp",EDGE,"E30.top"),sQuery(id+"F7.wireOp",EDGE,"E30.left"),sQuery(id+"F7.wireOp",EDGE,"E30.right")])],"isStart":false});
            var Q2;
            Q2=makeQuery(id+"F9.opExtrude","CAP_FACE",FACE,{"disambiguationData":[OSD([sQuery(id+"F7.wireOp",EDGE,"E21.bottom"),sQuery(id+"F7.wireOp",EDGE,"E21.top"),sQuery(id+"F7.wireOp",EDGE,"E21.left"),sQuery(id+"F7.wireOp",EDGE,"E21.right")])],"isStart":false});
            var Q3;
            Q3=makeQuery(id+"F11.opExtrude","CAP_FACE",FACE,{"disambiguationData":[OSD([sQuery(id+"F7.wireOp",EDGE,"E23.bottom"),sQuery(id+"F7.wireOp",EDGE,"E23.top"),sQuery(id+"F7.wireOp",EDGE,"E23.left"),sQuery(id+"F7.wireOp",EDGE,"E23.right")])],"isStart":false});
            var Q4;
            Q4=makeQuery(id+"F11.opExtrude","CAP_FACE",FACE,{"disambiguationData":[OSD([sQuery(id+"F7.wireOp",EDGE,"E27.bottom"),sQuery(id+"F7.wireOp",EDGE,"E27.top"),sQuery(id+"F7.wireOp",EDGE,"E27.left"),sQuery(id+"F7.wireOp",EDGE,"E27.right")])],"isStart":false});
            var Q5;
            Q5=makeQuery(id+"F9.opExtrude","CAP_FACE",FACE,{"disambiguationData":[OSD([sQuery(id+"F7.wireOp",EDGE,"E48.bottom"),sQuery(id+"F7.wireOp",EDGE,"E48.top"),sQuery(id+"F7.wireOp",EDGE,"E48.left"),sQuery(id+"F7.wireOp",EDGE,"E48.right")])],"isStart":false});
            var Q6;
            Q6=makeQuery(id+"F11.opExtrude","CAP_FACE",FACE,{"disambiguationData":[OSD([sQuery(id+"F7.wireOp",EDGE,"E31.bottom"),sQuery(id+"F7.wireOp",EDGE,"E31.top"),sQuery(id+"F7.wireOp",EDGE,"E31.left"),sQuery(id+"F7.wireOp",EDGE,"E31.right")])],"isStart":false});
            var Q7;
            Q7=makeQuery(id+"F10.opExtrude","CAP_FACE",FACE,{"disambiguationData":[OSD([sQuery(id+"F7.wireOp",EDGE,"E35.bottom"),sQuery(id+"F7.wireOp",EDGE,"E35.top"),sQuery(id+"F7.wireOp",EDGE,"E35.left"),sQuery(id+"F7.wireOp",EDGE,"E35.right")])],"isStart":false});
            var Q8;
            Q8=makeQuery(id+"F10.opExtrude","CAP_FACE",FACE,{"disambiguationData":[OSD([sQuery(id+"F7.wireOp",EDGE,"E37.bottom"),sQuery(id+"F7.wireOp",EDGE,"E37.top"),sQuery(id+"F7.wireOp",EDGE,"E37.left"),sQuery(id+"F7.wireOp",EDGE,"E37.right")])],"isStart":false});
            var Q9;
            Q9=makeQuery(id+"F10.opExtrude","CAP_FACE",FACE,{"disambiguationData":[OSD([sQuery(id+"F7.wireOp",EDGE,"E39.bottom"),sQuery(id+"F7.wireOp",EDGE,"E39.top"),sQuery(id+"F7.wireOp",EDGE,"E39.left"),sQuery(id+"F7.wireOp",EDGE,"E39.right")])],"isStart":false});
            var Q10;
            Q10=makeQuery(id+"F10.opExtrude","CAP_FACE",FACE,{"disambiguationData":[OSD([sQuery(id+"F7.wireOp",EDGE,"E41.bottom"),sQuery(id+"F7.wireOp",EDGE,"E41.top"),sQuery(id+"F7.wireOp",EDGE,"E41.left"),sQuery(id+"F7.wireOp",EDGE,"E41.right")])],"isStart":false});
            var Q11;
            Q11=makeQuery(id+"F10.opExtrude","CAP_FACE",FACE,{"disambiguationData":[OSD([sQuery(id+"F7.wireOp",EDGE,"E43.bottom"),sQuery(id+"F7.wireOp",EDGE,"E43.top"),sQuery(id+"F7.wireOp",EDGE,"E43.left"),sQuery(id+"F7.wireOp",EDGE,"E43.right")])],"isStart":false});
            var Q12;
            Q12=makeQuery(id+"F10.opExtrude","CAP_FACE",FACE,{"disambiguationData":[OSD([sQuery(id+"F7.wireOp",EDGE,"E45.bottom"),sQuery(id+"F7.wireOp",EDGE,"E45.top"),sQuery(id+"F7.wireOp",EDGE,"E45.left"),sQuery(id+"F7.wireOp",EDGE,"E45.right")])],"isStart":false});
            var Q13;
            Q13=makeQuery(id+"F10.opExtrude","CAP_FACE",FACE,{"disambiguationData":[OSD([sQuery(id+"F7.wireOp",EDGE,"E47.bottom"),sQuery(id+"F7.wireOp",EDGE,"E47.top"),sQuery(id+"F7.wireOp",EDGE,"E47.left"),sQuery(id+"F7.wireOp",EDGE,"E47.right")])],"isStart":false});
            var Q14;
            Q14=makeQuery(id+"F11.opExtrude","CAP_FACE",FACE,{"disambiguationData":[OSD([sQuery(id+"F7.wireOp",EDGE,"E21.bottom"),sQuery(id+"F7.wireOp",EDGE,"E21.top"),sQuery(id+"F7.wireOp",EDGE,"E21.left"),sQuery(id+"F7.wireOp",EDGE,"E21.right")])],"isStart":false});
            fillet(context, id + "F13", {"entities" : qUnion([Q0, Q1, Q2, Q3, Q4, Q5, Q6, Q7, Q8, Q9, Q10, Q11, Q12, Q13, Q14]), "radius" : 1.5 * mm, "tangentPropagation" : true, "allowEdgeOverflow" : false});
        }
        {
            var Q0;
            Q0=makeQuery(id+"F1.opExtrude","CAP_FACE",FACE,{"disambiguationData":[OSD([sQuery(id+"F0.wireOp",EDGE,"E0.bottom"),sQuery(id+"F0.wireOp",EDGE,"E0.top"),sQuery(id+"F0.wireOp",EDGE,"E0.left"),sQuery(id+"F0.wireOp",EDGE,"E0.right"),sQuery(id+"F0.wireOp",EDGE,"E2")])],"isStart":true});
            fillet(context, id + "F14", {"entities" : qUnion([Q0]), "radius" : 2 * mm, "tangentPropagation" : true, "allowEdgeOverflow" : false});
        }
    });
